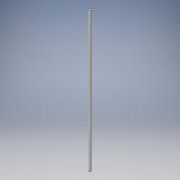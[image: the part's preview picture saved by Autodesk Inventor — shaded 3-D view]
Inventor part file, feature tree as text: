
AUTODESK INVENTOR PART (.ipt)
format: ipt  version: 2016 (Build 200138000, 138)  size: 84,480 bytes
history: native  units: in
note: dims shown in document units (in); Inventor stores cm internally (conversion verified against a paired STEP export)
features: extrude x1, sketch x1
ambient origin geometry x8: Origin, YZ Plane, XZ Plane, XY Plane, X Axis, Y Axis, Z Axis, Center Point
bodies: Solid1 (feature_tree)
feature tree (2):
  extrude  "Extrusion1"  Depth=14.0in TaperAngle=0.0deg
  sketch  "Sketch1"  dims[d0=0.25in d1=14.0in d2=0.0in]
